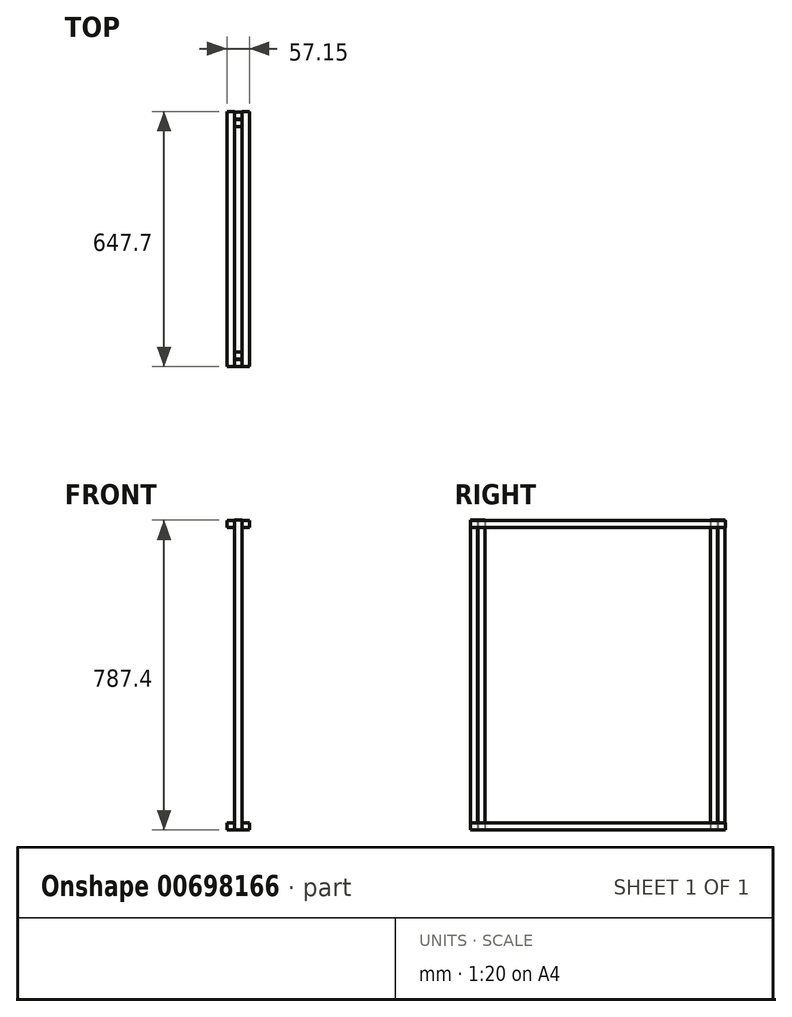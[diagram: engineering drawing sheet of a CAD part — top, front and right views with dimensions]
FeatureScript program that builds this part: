
annotation { "Feature Type Name" : "Feature", "Feature Type Description" : "" }
export const myFeature = defineFeature(function(context is Context, id is Id, definition is map)
    precondition{}
    {
        {
            var Q0;
            Q0=qCreatedBy(makeId("Top.planeOp"),FACE);
            var sketch = newSketch(context, id + "F0", { "sketchPlane" : qUnion([Q0])});
            skLineSegment(sketch, "E0.bottom", {"start": v(0, 0) * mm, "end": v(19.05, 0) * mm});
            skLineSegment(sketch, "E0.top", {"start": v(0, 17.78) * mm, "end": v(19.05, 17.78) * mm});
            skLineSegment(sketch, "E0.left", {"start": v(0, 0) * mm, "end": v(0, 17.78) * mm});
            skLineSegment(sketch, "E0.right", {"start": v(19.05, 0) * mm, "end": v(19.05, 17.78) * mm});
            skSolve(sketch);
        }
        {
            var Q0;
            Q0=makeQuery(id+"F0.imprint","IMPRINT",FACE,{"disambiguationData":[TD([[makeQuery(id+"F0.imprint","IMPRINT",EDGE,{"derivedFrom":sQuery(id+"F0.wireOp",EDGE,"E0.bottom")}),1.0]])]});
            extrude(context, id + "F1", {"entities" : qUnion([Q0]), "depth" : 787.4 * mm, "offsetDistance" : 25.4 * mm});
        }
        {
            var Q0;
            Q0=makeQuery(id+"F1.opExtrude","SWEPT_BODY",BODY,{"disambiguationData":[OSD([sQuery(id+"F0.wireOp",EDGE,"E0.bottom"),sQuery(id+"F0.wireOp",EDGE,"E0.top"),sQuery(id+"F0.wireOp",EDGE,"E0.left"),sQuery(id+"F0.wireOp",EDGE,"E0.right")])]});
            transform(context, id + "F2", {"entities" : qUnion([Q0]), "transformType" : TransformType.TRANSLATION_3D, "dx" : 0 * mm, "dy" : 19.05 * mm, "dz" : 0 * mm, "makeCopy" : true});
        }
        {
            var Q0;
            Q0=makeQuery(id+"F1.opExtrude","SWEPT_BODY",BODY,{"disambiguationData":[OSD([sQuery(id+"F0.wireOp",EDGE,"E0.bottom"),sQuery(id+"F0.wireOp",EDGE,"E0.top"),sQuery(id+"F0.wireOp",EDGE,"E0.left"),sQuery(id+"F0.wireOp",EDGE,"E0.right")])]});
            transform(context, id + "F3", {"entities" : qUnion([Q0]), "transformType" : TransformType.TRANSLATION_3D, "dx" : 0 * mm, "dy" : 609.6 * mm, "dz" : 0 * mm, "makeCopy" : true});
        }
        {
            var Q0;
            Q0=makeQuery(id+"F2.opPattern","COPY",BODY,{"derivedFrom":makeQuery(id+"F1.opExtrude","SWEPT_BODY",BODY,{"disambiguationData":[OSD([sQuery(id+"F0.wireOp",EDGE,"E0.bottom"),sQuery(id+"F0.wireOp",EDGE,"E0.top"),sQuery(id+"F0.wireOp",EDGE,"E0.left"),sQuery(id+"F0.wireOp",EDGE,"E0.right")])]}),"instanceName":"1"});
            transform(context, id + "F4", {"entities" : qUnion([Q0]), "transformType" : TransformType.TRANSLATION_3D, "dx" : 0 * mm, "dy" : 609.6 * mm, "dz" : 0 * mm, "makeCopy" : true});
        }
        {
            var Q0;
            Q0=qCreatedBy(makeId("Front.planeOp"),FACE);
            var sketch = newSketch(context, id + "F5", { "sketchPlane" : qUnion([Q0])});
            skLineSegment(sketch, "E1.bottom", {"start": v(0, 0) * mm, "end": v(-19.05, 0) * mm});
            skLineSegment(sketch, "E1.top", {"start": v(0, 17.42) * mm, "end": v(-19.05, 17.42) * mm});
            skLineSegment(sketch, "E1.left", {"start": v(0, 0) * mm, "end": v(0, 17.42) * mm});
            skLineSegment(sketch, "E1.right", {"start": v(-19.05, 0) * mm, "end": v(-19.05, 17.42) * mm});
            skSolve(sketch);
        }
        {
            var Q0;
            Q0=makeQuery(id+"F5.imprint","IMPRINT",FACE,{"disambiguationData":[TD([[makeQuery(id+"F5.imprint","IMPRINT",EDGE,{"derivedFrom":sQuery(id+"F5.wireOp",EDGE,"E1.bottom")}),-1.0]])]});
            extrude(context, id + "F6", {"entities" : qUnion([Q0]), "depth" : -647.7 * mm, "offsetDistance" : 25.4 * mm});
        }
        {
            var Q0;
            Q0=makeQuery(id+"F6.opExtrude","SWEPT_BODY",BODY,{"disambiguationData":[OSD([sQuery(id+"F5.wireOp",EDGE,"E1.bottom"),sQuery(id+"F5.wireOp",EDGE,"E1.top"),sQuery(id+"F5.wireOp",EDGE,"E1.left"),sQuery(id+"F5.wireOp",EDGE,"E1.right")])]});
            transform(context, id + "F7", {"entities" : qUnion([Q0]), "transformType" : TransformType.TRANSLATION_3D, "dx" : 38.1 * mm, "dy" : 0 * mm, "dz" : 0 * mm, "makeCopy" : true});
        }
        {
            var Q0;
            Q0=makeQuery(id+"F7.opPattern","COPY",BODY,{"derivedFrom":makeQuery(id+"F6.opExtrude","SWEPT_BODY",BODY,{"disambiguationData":[OSD([sQuery(id+"F5.wireOp",EDGE,"E1.bottom"),sQuery(id+"F5.wireOp",EDGE,"E1.top"),sQuery(id+"F5.wireOp",EDGE,"E1.left"),sQuery(id+"F5.wireOp",EDGE,"E1.right")])]}),"instanceName":"1"});
            transform(context, id + "F8", {"entities" : qUnion([Q0]), "transformType" : TransformType.TRANSLATION_3D, "dx" : 0 * mm, "dy" : 0 * mm, "dz" : 768.35 * mm, "makeCopy" : true});
        }
        {
            var Q0;
            Q0=makeQuery(id+"F6.opExtrude","SWEPT_BODY",BODY,{"disambiguationData":[OSD([sQuery(id+"F5.wireOp",EDGE,"E1.bottom"),sQuery(id+"F5.wireOp",EDGE,"E1.top"),sQuery(id+"F5.wireOp",EDGE,"E1.left"),sQuery(id+"F5.wireOp",EDGE,"E1.right")])]});
            transform(context, id + "F9", {"entities" : qUnion([Q0]), "transformType" : TransformType.TRANSLATION_3D, "dx" : 0 * mm, "dy" : 0 * mm, "dz" : 768.35 * mm, "makeCopy" : true});
        }
    });
